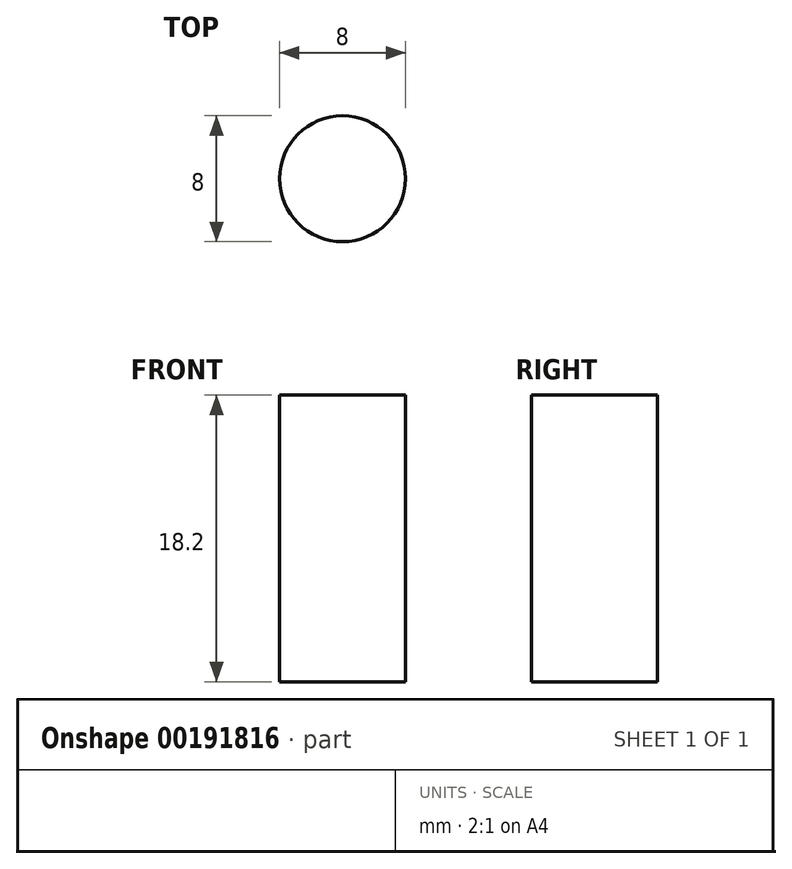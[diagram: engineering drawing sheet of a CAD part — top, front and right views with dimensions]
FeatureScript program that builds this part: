
annotation { "Feature Type Name" : "Feature", "Feature Type Description" : "" }
export const myFeature = defineFeature(function(context is Context, id is Id, definition is map)
    precondition{}
    {
        {
            var Q0;
            Q0=qCreatedBy(makeId("Top.planeOp"),FACE);
            var sketch = newSketch(context, id + "F0", { "sketchPlane" : qUnion([Q0])});
            skCircle(sketch, "E0", {"center": v(0, 0) * mm, "radius": 4 * mm});
            skSolve(sketch);
        }
        {
            var Q0;
            Q0=makeQuery(id+"F0.imprint","IMPRINT",FACE,{"disambiguationData":[TD([[makeQuery(id+"F0.imprint","IMPRINT",EDGE,{"derivedFrom":sQuery(id+"F0.wireOp",EDGE,"E0")}),1.0]])]});
            extrude(context, id + "F1", {"entities" : qUnion([Q0]), "depth" : 18.2 * mm});
        }
    });
